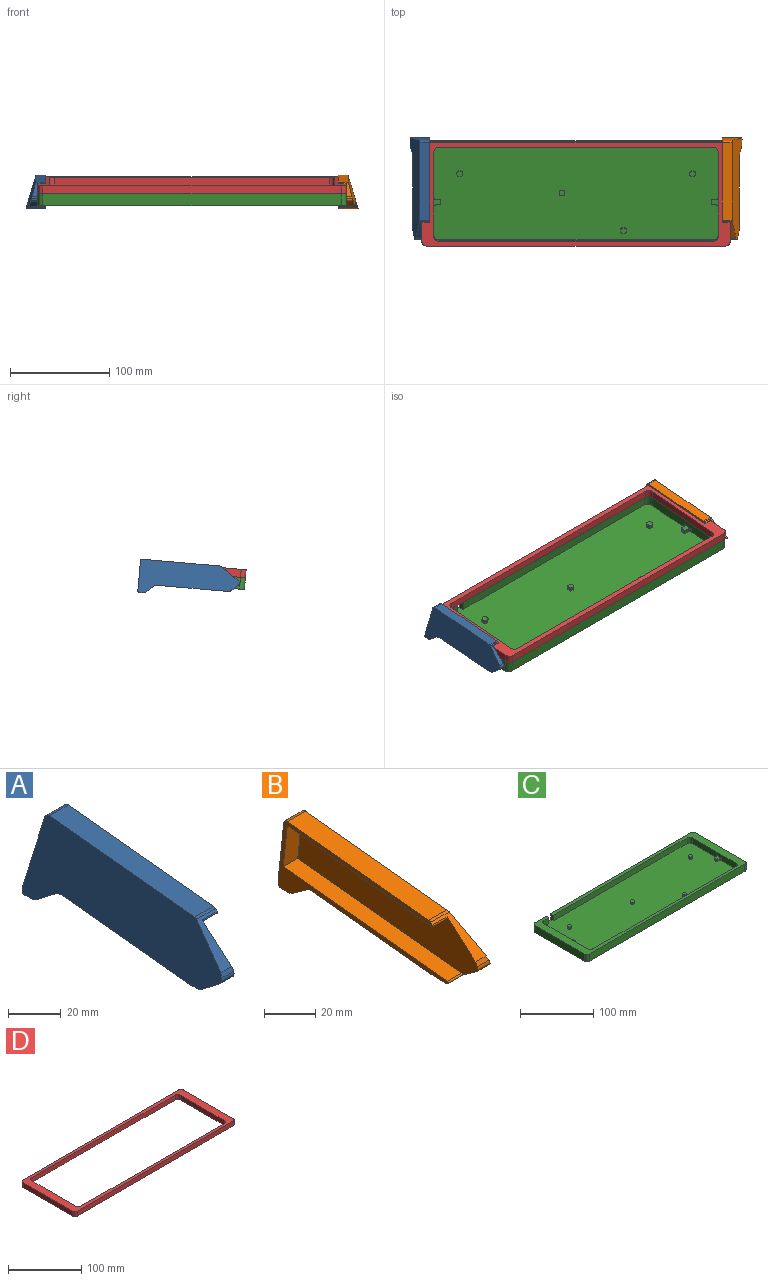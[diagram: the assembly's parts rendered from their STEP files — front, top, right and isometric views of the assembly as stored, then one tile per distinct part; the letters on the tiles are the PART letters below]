
ASSEMBLY  parts=4 mates=8
PART A: 25 faces, bbox 19.9x102.6x33.8 mm
  f0: plane 94.22x33.76mm, normal (1,0,0), area 494.7mm2, adj f1,f3,f4,f6,f7,f8,f9,f11
  f1: plane 19.93x3.4mm, normal (0,0,-1), area 67.6mm2, adj f0,f2,f19,f24
  f2: plane 102.62x33.77mm, normal (-0.96,-0.03,0.28), area 2549.8mm2, adj f1,f3,f4,f5,f6,f11,f12,f15
  f3: plane 17.27x4.14mm, normal (0,0,-1), area 71.2mm2, adj f0,f2,f16,f23
  f4: plane 78.12x9.97mm, normal (0,-0.1,0.99), area 782.8mm2, adj f0,f2,f17,f18
  f5: plane 6.31x1.77mm, normal (0,-0.87,0.5), area 12.4mm2, adj f2,f10,f11,f15
  f6: plane 29.76x19.35mm, normal (0,0.99,0.1), area 447.4mm2, adj f0,f2,f18,f19
  f7: plane 80.01x8.41mm, normal (0,0.1,-0.99), area 643.6mm2, adj f0,f9,f10,f14
  f8: plane 90.83x9.55mm, normal (0,-0.1,0.99), area 730.6mm2, adj f0,f9,f10,f13
  f9: plane 20.79x8mm, normal (0,-0.99,-0.1), area 167.2mm2, adj f0,f7,f8,f10
  f10: plane 99.68x31.24mm, normal (1,0,0), area 1951.6mm2, adj f5,f7,f8,f9,f11,f12,f13,f14
  f11: plane 16.76x14.6mm, normal (0,-0.66,0.75), area 97.9mm2, adj f0,f2,f5,f10,f14,f17
  f12: plane 17x7.98mm, normal (0,-0.58,-0.81), area 81mm2, adj f0,f2,f10,f13,f15,f16
  f13: cylinder r=0.5mm len=8mm, axis (1,0,0), area 9.7mm2, adj f0,f8,f10,f12
  f14: cylinder r=0.5mm len=8mm, axis (-1,0,0), area 10.1mm2, adj f0,f7,f10,f11
  f15: cylinder r=2mm len=7.1mm, axis (1,0,0), area 19.8mm2, adj f2,f5,f10,f12
  f16: cylinder r=2mm len=17.15mm, axis (1,0,0), area 21.2mm2, adj f0,f2,f3,f12
  f17: cylinder r=2mm len=10.07mm, axis (1,0,0), area 12.2mm2, adj f0,f2,f4,f11
  f18: cylinder r=2mm len=10.55mm, axis (1,0,0), area 32mm2, adj f0,f2,f4,f6
  f19: cylinder r=2mm len=19.94mm, axis (1,0,0), area 66.1mm2, adj f0,f1,f2,f6
  f20: plane 19.47x7.6mm, normal (0,-0.58,-0.81), area 173.1mm2, adj f0,f2,f22,f24
  f21: plane 68.65x17.28mm, normal (0,0.1,-0.99), area 1193mm2, adj f0,f2,f22,f23
  f22: cylinder r=5mm len=17.65mm, axis (1,0,0), area 63mm2, adj f0,f2,f20,f21
  f23: cylinder r=5mm len=17.28mm, axis (1,0,0), area 9mm2, adj f0,f2,f3,f21
  f24: cylinder r=5mm len=19.83mm, axis (-1,0,0), area 61mm2, adj f0,f1,f2,f20
PART B: 25 faces, bbox 19.9x102.6x33.8 mm
  f0: plane 94.22x33.76mm, normal (-1,0,0), area 494.7mm2, adj f1,f3,f4,f6,f7,f8,f9,f11
  f1: plane 19.93x3.4mm, normal (0,0,-1), area 67.6mm2, adj f0,f2,f19,f24
  f2: plane 102.62x33.77mm, normal (0.96,-0.03,0.28), area 2549.8mm2, adj f1,f3,f4,f5,f6,f11,f12,f15
  f3: plane 17.27x4.14mm, normal (0,0,-1), area 71.2mm2, adj f0,f2,f16,f23
  f4: plane 78.12x9.97mm, normal (0,-0.1,0.99), area 782.8mm2, adj f0,f2,f17,f18
  f5: plane 6.31x1.77mm, normal (0,-0.87,0.5), area 12.4mm2, adj f2,f10,f11,f15
  f6: plane 29.76x19.35mm, normal (0,0.99,0.1), area 447.4mm2, adj f0,f2,f18,f19
  f7: plane 80.01x8.41mm, normal (0,0.1,-0.99), area 643.6mm2, adj f0,f9,f10,f14
  f8: plane 90.83x9.55mm, normal (0,-0.1,0.99), area 730.6mm2, adj f0,f9,f10,f13
  f9: plane 20.79x8mm, normal (0,-0.99,-0.1), area 167.2mm2, adj f0,f7,f8,f10
  f10: plane 99.68x31.24mm, normal (-1,0,0), area 1951.6mm2, adj f5,f7,f8,f9,f11,f12,f13,f14
  f11: plane 16.76x14.6mm, normal (0,-0.66,0.75), area 97.9mm2, adj f0,f2,f5,f10,f14,f17
  f12: plane 17x7.98mm, normal (0,-0.58,-0.81), area 81mm2, adj f0,f2,f10,f13,f15,f16
  f13: cylinder r=0.5mm len=8mm, axis (-1,0,0), area 9.7mm2, adj f0,f8,f10,f12
  f14: cylinder r=0.5mm len=8mm, axis (1,0,0), area 10.1mm2, adj f0,f7,f10,f11
  f15: cylinder r=2mm len=7.1mm, axis (-1,0,0), area 19.8mm2, adj f2,f5,f10,f12
  f16: cylinder r=2mm len=17.15mm, axis (-1,0,0), area 21.2mm2, adj f0,f2,f3,f12
  f17: cylinder r=2mm len=10.07mm, axis (-1,0,0), area 12.2mm2, adj f0,f2,f4,f11
  f18: cylinder r=2mm len=10.55mm, axis (-1,0,0), area 32mm2, adj f0,f2,f4,f6
  f19: cylinder r=2mm len=19.94mm, axis (-1,0,0), area 66.1mm2, adj f0,f1,f2,f6
  f20: plane 19.47x7.6mm, normal (0,-0.58,-0.81), area 173.1mm2, adj f0,f2,f22,f24
  f21: plane 68.65x17.28mm, normal (0,0.1,-0.99), area 1193mm2, adj f0,f2,f22,f23
  f22: cylinder r=5mm len=17.65mm, axis (-1,0,0), area 63mm2, adj f0,f2,f20,f21
  f23: cylinder r=5mm len=17.28mm, axis (-1,0,0), area 9mm2, adj f0,f2,f3,f21
  f24: cylinder r=5mm len=19.83mm, axis (1,0,0), area 61mm2, adj f0,f1,f2,f20
PART C: 74 faces, bbox 311x105x12 mm
  f0: plane 9.5x9.5mm, normal (0,-1,0), area 90.2mm2, adj f1,f7,f11,f72
  f1: plane 311x105mm, normal (0,0,1), area 5347.5mm2, adj f0,f2,f3,f4,f5,f6,f7,f8
  f2: plane 301x12mm, normal (0,1,0), area 3531.2mm2, adj f1,f11,f64,f65,f68,f72,f73
  f3: plane 85x9.5mm, normal (1,0,0), area 769.5mm2, adj f1,f7,f8,f11,f34,f46,f47
  f4: plane 259x9.5mm, normal (0,-1,0), area 2460.5mm2, adj f1,f10,f11,f73
  f5: plane 277x9.5mm, normal (0,1,0), area 2631.5mm2, adj f1,f8,f9,f11
  f6: plane 85x9.5mm, normal (-1,0,0), area 769.5mm2, adj f1,f9,f10,f11,f30,f48,f49
  f7: cylinder r=5mm len=9.5mm, axis (0,0,1), area 74.6mm2, adj f0,f1,f3,f11
  f8: cylinder r=5mm len=9.5mm, axis (0,0,-1), area 74.6mm2, adj f1,f3,f5,f11
  f9: cylinder r=5mm len=9.5mm, axis (0,0,1), area 74.6mm2, adj f1,f5,f6,f11
  f10: cylinder r=5mm len=9.5mm, axis (0,0,-1), area 74.6mm2, adj f1,f4,f6,f11
  f11: plane 287x100mm, normal (0,0,1), area 27101.2mm2, adj f0,f2,f3,f4,f5,f6,f7,f8
  f12: plane 4x1.5mm, normal (0,1,0), area 6mm2, adj f11,f16,f60,f63
  f13: plane 4x1.5mm, normal (-1,0,0), area 6mm2, adj f11,f16,f62,f63
  f14: plane 4x1.5mm, normal (0,-1,0), area 6mm2, adj f11,f16,f61,f62
  f15: plane 4x1.5mm, normal (1,0,0), area 6mm2, adj f11,f16,f60,f61
  f16: plane 5.5x5.5mm, normal (0,0,1), area 26.8mm2, adj f12,f13,f14,f15,f60,f61,f62,f63
  f17: plane 4x1.5mm, normal (0,1,0), area 6mm2, adj f11,f21,f56,f59
  f18: plane 4x1.5mm, normal (-1,0,0), area 6mm2, adj f11,f21,f56,f57
  f19: plane 4x1.5mm, normal (0,-1,0), area 6mm2, adj f11,f21,f57,f58
  f20: plane 4x1.5mm, normal (1,0,0), area 6mm2, adj f11,f21,f58,f59
  f21: plane 5.5x5.5mm, normal (0,0,1), area 26.8mm2, adj f17,f18,f19,f20,f56,f57,f58,f59
  f22: plane 4x1.5mm, normal (0,1,0), area 6mm2, adj f11,f26,f52,f55
  f23: plane 4x1.5mm, normal (-1,0,0), area 6mm2, adj f11,f26,f54,f55
  f24: plane 4x1.5mm, normal (0,-1,0), area 6mm2, adj f11,f26,f53,f54
  f25: plane 4x1.5mm, normal (1,0,0), area 6mm2, adj f11,f26,f52,f53
  f26: plane 5.5x5.5mm, normal (0,0,1), area 26.8mm2, adj f22,f23,f24,f25,f52,f53,f54,f55
  f27: plane 4x3.05mm, normal (0,1,0), area 12.2mm2, adj f11,f30,f48,f51
  f28: plane 4x1.5mm, normal (-1,0,0), area 6mm2, adj f11,f30,f50,f51
  f29: plane 4x3.05mm, normal (0,-1,0), area 12.2mm2, adj f11,f30,f49,f50
  f30: plane 9.5x7.05mm, normal (0,0,1), area 38.8mm2, adj f6,f27,f28,f29,f48,f49,f50,f51
  f31: plane 4x3.05mm, normal (0,1,0), area 12.2mm2, adj f11,f34,f44,f47
  f32: plane 4x3.05mm, normal (0,-1,0), area 12.2mm2, adj f11,f34,f45,f46
  f33: plane 4x1.5mm, normal (1,0,0), area 6mm2, adj f11,f34,f44,f45
  f34: plane 9.5x7.05mm, normal (0,0,1), area 38.8mm2, adj f3,f31,f32,f33,f44,f45,f46,f47
  f35: plane 4x1.5mm, normal (0,1,0), area 6mm2, adj f11,f39,f40,f43
  f36: plane 4x1.5mm, normal (-1,0,0), area 6mm2, adj f11,f39,f42,f43
  f37: plane 4x1.5mm, normal (0,-1,0), area 6mm2, adj f11,f39,f41,f42
  f38: plane 4x1.5mm, normal (1,0,0), area 6mm2, adj f11,f39,f40,f41
  f39: plane 5.5x5.5mm, normal (0,0,1), area 26.8mm2, adj f35,f36,f37,f38,f40,f41,f42,f43
  f40: cylinder r=2mm len=4mm, axis (0,0,-1), area 12.6mm2, adj f11,f35,f38,f39
  f41: cylinder r=2mm len=4mm, axis (0,0,1), area 12.6mm2, adj f11,f37,f38,f39
  f42: cylinder r=2mm len=4mm, axis (0,0,-1), area 12.6mm2, adj f11,f36,f37,f39
  f43: cylinder r=2mm len=4mm, axis (0,0,1), area 12.6mm2, adj f11,f35,f36,f39
  f44: cylinder r=2mm len=4mm, axis (0,0,-1), area 12.6mm2, adj f11,f31,f33,f34
  f45: cylinder r=2mm len=4mm, axis (0,0,1), area 12.6mm2, adj f11,f32,f33,f34
  f46: cylinder r=2mm len=4mm, axis (0,0,1), area 12.6mm2, adj f3,f11,f32,f34
  f47: cylinder r=2mm len=4mm, axis (0,0,-1), area 12.6mm2, adj f3,f11,f31,f34
  f48: cylinder r=2mm len=4mm, axis (0,0,1), area 12.6mm2, adj f6,f11,f27,f30
  f49: cylinder r=2mm len=4mm, axis (0,0,-1), area 12.6mm2, adj f6,f11,f29,f30
  f50: cylinder r=2mm len=4mm, axis (0,0,-1), area 12.6mm2, adj f11,f28,f29,f30
  f51: cylinder r=2mm len=4mm, axis (0,0,1), area 12.6mm2, adj f11,f27,f28,f30
  f52: cylinder r=2mm len=4mm, axis (0,0,-1), area 12.6mm2, adj f11,f22,f25,f26
  f53: cylinder r=2mm len=4mm, axis (0,0,1), area 12.6mm2, adj f11,f24,f25,f26
  f54: cylinder r=2mm len=4mm, axis (0,0,-1), area 12.6mm2, adj f11,f23,f24,f26
  f55: cylinder r=2mm len=4mm, axis (0,0,1), area 12.6mm2, adj f11,f22,f23,f26
  f56: cylinder r=2mm len=4mm, axis (0,0,1), area 12.6mm2, adj f11,f17,f18,f21
  f57: cylinder r=2mm len=4mm, axis (0,0,-1), area 12.6mm2, adj f11,f18,f19,f21
  f58: cylinder r=2mm len=4mm, axis (0,0,1), area 12.6mm2, adj f11,f19,f20,f21
  f59: cylinder r=2mm len=4mm, axis (0,0,-1), area 12.6mm2, adj f11,f17,f20,f21
  f60: cylinder r=2mm len=4mm, axis (0,0,-1), area 12.6mm2, adj f11,f12,f15,f16
  f61: cylinder r=2mm len=4mm, axis (0,0,1), area 12.6mm2, adj f11,f14,f15,f16
  f62: cylinder r=2mm len=4mm, axis (0,0,-1), area 12.6mm2, adj f11,f13,f14,f16
  f63: cylinder r=2mm len=4mm, axis (0,0,1), area 12.6mm2, adj f11,f12,f13,f16
  f64: plane 311x105mm, normal (0,0,-1), area 32633.5mm2, adj f2,f65,f66,f67,f68,f69,f70,f71
  f65: cylinder r=5mm len=12mm, axis (0,0,1), area 94.2mm2, adj f1,f2,f64,f67
  f66: cylinder r=5mm len=12mm, axis (0,0,-1), area 94.2mm2, adj f1,f64,f67,f71
  f67: plane 95x12mm, normal (1,0,0), area 1140mm2, adj f1,f64,f65,f66
  f68: cylinder r=5mm len=12mm, axis (0,0,-1), area 94.2mm2, adj f1,f2,f64,f70
  f69: cylinder r=5mm len=12mm, axis (0,0,1), area 94.2mm2, adj f1,f64,f70,f71
  f70: plane 95x12mm, normal (-1,0,0), area 1140mm2, adj f1,f64,f68,f69
  f71: plane 301x12mm, normal (0,-1,0), area 3612mm2, adj f1,f64,f66,f69
  f72: plane 9.5x5mm, normal (1,0,0), area 47.5mm2, adj f0,f1,f2,f11
  f73: plane 9.5x5mm, normal (-1,0,0), area 47.5mm2, adj f1,f2,f4,f11
PART D: 18 faces, bbox 311x105x8 mm
  f0: cylinder r=5mm len=8mm, axis (0,0,1), area 62.8mm2, adj f6,f7,f8,f17
  f1: cylinder r=5mm len=8mm, axis (0,0,-1), area 62.8mm2, adj f5,f7,f8,f17
  f2: cylinder r=5mm len=8mm, axis (0,0,-1), area 62.8mm2, adj f4,f6,f8,f17
  f3: cylinder r=5mm len=8mm, axis (0,0,1), area 62.8mm2, adj f4,f5,f8,f17
  f4: plane 85x8mm, normal (-1,0,0), area 680mm2, adj f2,f3,f8,f17
  f5: plane 277x8mm, normal (0,1,0), area 2216mm2, adj f1,f3,f8,f17
  f6: plane 277x8mm, normal (0,-1,0), area 2216mm2, adj f0,f2,f8,f17
  f7: plane 85x8mm, normal (1,0,0), area 680mm2, adj f0,f1,f8,f17
  f8: plane 311x105mm, normal (0,0,1), area 5390mm2, adj f0,f1,f2,f3,f4,f5,f6,f7
  f9: cylinder r=5mm len=8mm, axis (0,0,1), area 62.8mm2, adj f8,f11,f15,f17
  f10: cylinder r=5mm len=8mm, axis (0,0,-1), area 62.8mm2, adj f8,f11,f16,f17
  f11: plane 95x8mm, normal (1,0,0), area 760mm2, adj f8,f9,f10,f17
  f12: cylinder r=5mm len=8mm, axis (0,0,-1), area 62.8mm2, adj f8,f14,f15,f17
  f13: cylinder r=5mm len=8mm, axis (0,0,1), area 62.8mm2, adj f8,f14,f16,f17
  f14: plane 95x8mm, normal (-1,0,0), area 760mm2, adj f8,f12,f13,f17
  f15: plane 301x8mm, normal (0,1,0), area 2408mm2, adj f8,f9,f12,f17
  f16: plane 301x8mm, normal (0,-1,0), area 2408mm2, adj f8,f10,f13,f17
  f17: plane 311x105mm, normal (0,0,-1), area 5390mm2, adj f0,f1,f2,f3,f4,f5,f6,f7
PLACE A rot(axis=(-1,0,0),1deg) t=(-178.11,2.41,-7.14)mm
PLACE B rot(axis=(-1,0,0),1deg) t=(116.89,2.41,-7.14)mm
PLACE C rot(axis=(1,0,0),5deg) t=(-148.11,2.29,-5.75)mm
PLACE D rot(axis=(1,0,0),5deg) t=(-148.11,2.29,-5.75)mm
MATE planar D.f17 <-> C.f1  axis (0,0.09,-1) through (-156.11,53.54,10.78)mm
MATE planar D.f14 <-> C.f70  axis (-1,0,0) through (-156.11,53.19,14.76)mm
MATE planar B.f9 <-> C.f2  axis (0,-1,-0.09) through (150.89,106.1,12.42)mm
MATE planar A.f9 <-> C.f2  axis (0,-1,-0.09) through (-152.11,106.1,12.42)mm
MATE planar A.f21 <-> B.f21  axis (0,0.09,-1) through (-156.75,56.18,-4.44)mm
MATE planar D.f16 <-> C.f71  axis (0,-1,-0.09) through (-0.61,0.89,10.19)mm
MATE planar B.f10 <-> C.f67  axis (-1,0,0) through (154.89,59.47,8.08)mm
MATE planar A.f10 <-> C.f70  axis (1,0,0) through (-156.11,16.65,9.96)mm
